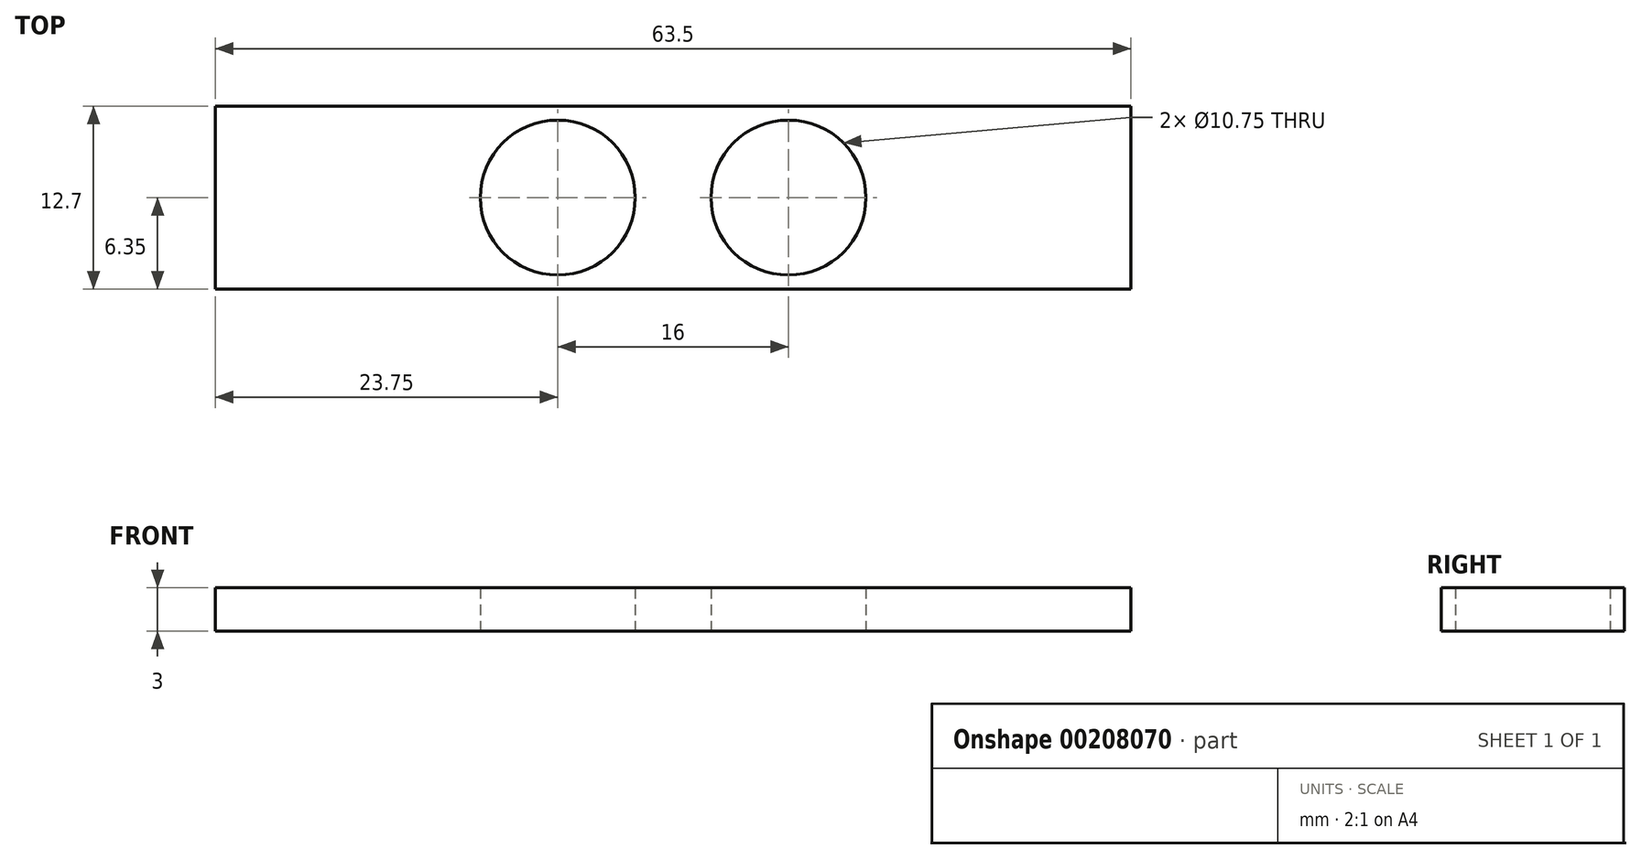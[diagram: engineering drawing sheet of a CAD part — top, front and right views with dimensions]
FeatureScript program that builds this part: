
annotation { "Feature Type Name" : "Feature", "Feature Type Description" : "" }
export const myFeature = defineFeature(function(context is Context, id is Id, definition is map)
    precondition{}
    {
        {
            var Q0;
            Q0=qCreatedBy(makeId("Top.planeOp"),FACE);
            var sketch = newSketch(context, id + "F0", { "sketchPlane" : qUnion([Q0])});
            skLineSegment(sketch, "E0.bottom", {"start": v(-31.75, -6.35) * mm, "end": v(31.75, -6.35) * mm});
            skLineSegment(sketch, "E0.top", {"start": v(-31.75, 6.35) * mm, "end": v(31.75, 6.35) * mm});
            skLineSegment(sketch, "E0.left", {"start": v(-31.75, -6.35) * mm, "end": v(-31.75, 6.35) * mm});
            skLineSegment(sketch, "E0.right", {"start": v(31.75, -6.35) * mm, "end": v(31.75, 6.35) * mm});
            skPoint(sketch, "E0.middle", {"position": v(0, 0) * mm});
            skPoint(sketch, "E1", {"position": v(-8, 0) * mm});
            skPoint(sketch, "E2.MirrorP", {"position": v(8, 0) * mm});
            skCircle(sketch, "E3", {"center": v(-8, 0) * mm, "radius": 5.38 * mm});
            skCircle(sketch, "E4.MirrorC", {"center": v(8, 0) * mm, "radius": 5.38 * mm});
            skPoint(sketch, "E5", {"position": v(13.38, 0) * mm});
            skPoint(sketch, "E6", {"position": v(31.75, 0) * mm});
            skSolve(sketch);
        }
        {
            var Q0;
            Q0=makeQuery(id+"F0.imprint","IMPRINT",FACE,{"disambiguationData":[TD([[makeQuery(id+"F0.imprint","IMPRINT",EDGE,{"derivedFrom":sQuery(id+"F0.wireOp",EDGE,"E0.bottom")}),1.0]])]});
            extrude(context, id + "F1", {"entities" : qUnion([Q0]), "depth" : 3 * mm});
        }
    });
